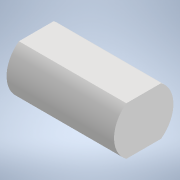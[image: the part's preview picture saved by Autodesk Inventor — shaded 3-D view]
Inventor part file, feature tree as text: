
AUTODESK INVENTOR PART (.ipt)
format: ipt  version: 2022 (Build 260153070, 153G)  size: 95,232 bytes
history: native  units: mm
features: other x3, extrude x1, sketch x1, reference x1
ambient origin geometry x8: Origin, YZ Plane, XZ Plane, XY Plane, X Axis, Y Axis, Z Axis, Center Point
bodies: Body1 (feature_tree)
feature tree (6):
  extrude  "Extrusion2"  Depth=15.0mm
  sketch  "Sketch1"  dims[d2=18.5mm d3=15.0mm d4=33.5mm d5=0.0mm]
  reference  "Reference1"
  other  "<userpath> laptop\Desktop\SumoBot\sumobotENCODER\MotorEncoderAssembly.iam"
  other  "MotorEncoderAssembly.iam"
  other  "TT motor output:1"
